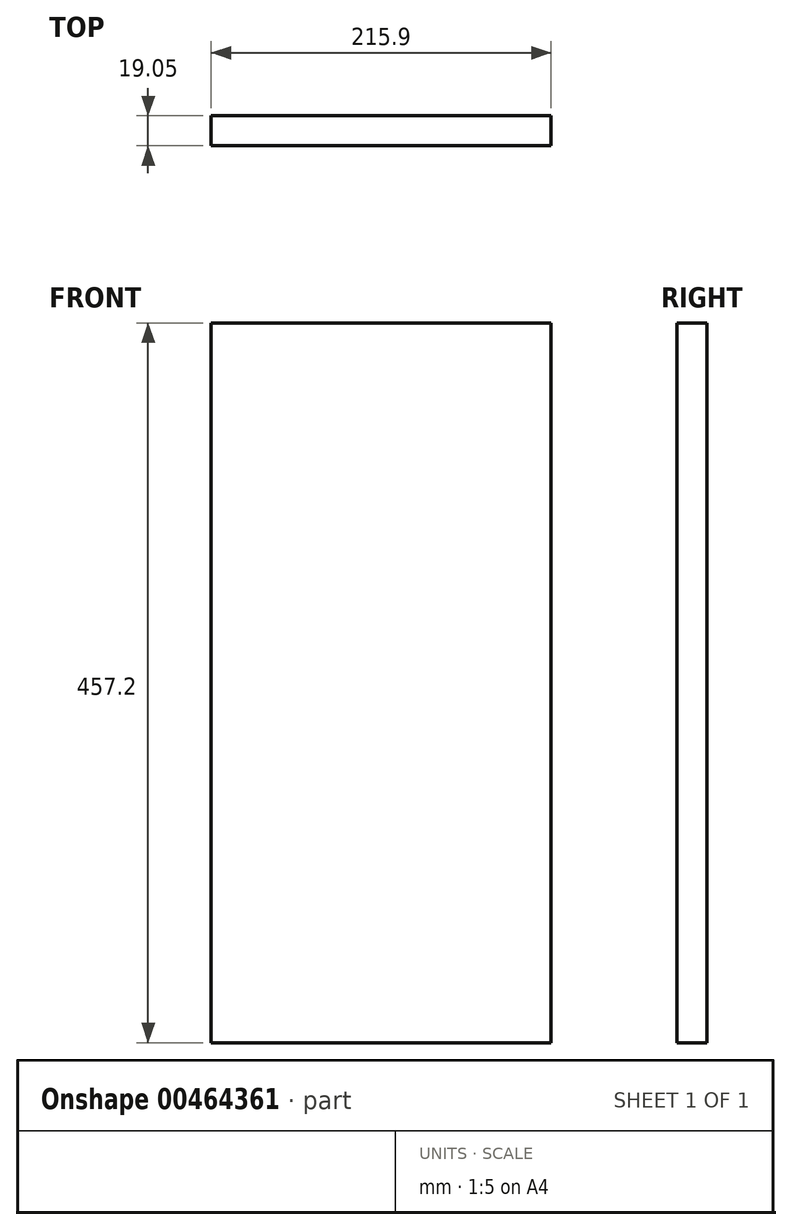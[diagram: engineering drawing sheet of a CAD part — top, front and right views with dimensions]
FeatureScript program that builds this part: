
annotation { "Feature Type Name" : "Feature", "Feature Type Description" : "" }
export const myFeature = defineFeature(function(context is Context, id is Id, definition is map)
    precondition{}
    {
        {
            var Q0;
            Q0=qCreatedBy(makeId("Front.planeOp"),FACE);
            var sketch = newSketch(context, id + "F0", { "sketchPlane" : qUnion([Q0])});
            skLineSegment(sketch, "E0", {"start": v(-104.24, 450.04) * mm, "end": v(111.66, 450.04) * mm});
            skLineSegment(sketch, "E1", {"start": v(-104.24, 450.04) * mm, "end": v(-104.24, -7.16) * mm});
            skLineSegment(sketch, "E2", {"start": v(-104.24, -7.16) * mm, "end": v(111.66, -7.16) * mm});
            skLineSegment(sketch, "E3", {"start": v(111.66, 450.04) * mm, "end": v(111.66, -7.16) * mm});
            skSolve(sketch);
        }
        {
            var Q0;
            Q0=makeQuery(id+"F0.imprint","IMPRINT",FACE,{"disambiguationData":[TD([[makeQuery(id+"F0.imprint","IMPRINT",EDGE,{"derivedFrom":sQuery(id+"F0.wireOp",EDGE,"E0")}),-1.0]])]});
            extrude(context, id + "F1", {"entities" : qUnion([Q0]), "depth" : 19.05 * mm});
        }
        {
            var Q0;
            Q0=makeQuery(id+"F1.opExtrude","CAP_FACE",FACE,{"disambiguationData":[OSD([sQuery(id+"F0.wireOp",EDGE,"E0"),sQuery(id+"F0.wireOp",EDGE,"E1"),sQuery(id+"F0.wireOp",EDGE,"E2"),sQuery(id+"F0.wireOp",EDGE,"E3")])],"isStart":false});
            var sketch = newSketch(context, id + "F2", { "sketchPlane" : qUnion([Q0])});
            skLineSegment(sketch, "E4", {"start": v(-89.44, 450.04) * mm, "end": v(-89.44, 340.58) * mm});
            skLineSegment(sketch, "E5", {"start": v(-89.44, 340.58) * mm, "end": v(92.64, 340.58) * mm});
            skLineSegment(sketch, "E6", {"start": v(92.64, 340.58) * mm, "end": v(92.64, 450.04) * mm});
            skSolve(sketch);
        }
        {
            var Q0;
            {var subQ0=sQuery(id+"F2.wireOp",EDGE,"E4");Q0=makeQuery(id+"F2.imprint","IMPRINT",FACE,{"disambiguationData":[TD([[makeQuery(id+"F2.imprint","IMPRINT",EDGE,{"derivedFrom":subQ0}),1.0]])]});}
            extrude(context, id + "F3", {"entities" : qUnion([Q0]), "operationType" : NewBodyOperationType.ADD, "depth" : -6.35 * mm});
        }
        {
            var Q0;
            Q0=makeQuery(id+"F1.opExtrude","CAP_FACE",FACE,{"disambiguationData":[OSD([sQuery(id+"F0.wireOp",EDGE,"E0"),sQuery(id+"F0.wireOp",EDGE,"E1"),sQuery(id+"F0.wireOp",EDGE,"E2"),sQuery(id+"F0.wireOp",EDGE,"E3")])],"isStart":false});
            var sketch = newSketch(context, id + "F4", { "sketchPlane" : qUnion([Q0])});
            skLineSegment(sketch, "E7", {"start": v(-92.07, 0) * mm, "end": v(96.33, 0) * mm});
            skLineSegment(sketch, "E8", {"start": v(96.33, 0) * mm, "end": v(96.33, 22.2) * mm});
            skLineSegment(sketch, "E9", {"start": v(96.33, 22.2) * mm, "end": v(-92.07, 22.2) * mm});
            skLineSegment(sketch, "E10", {"start": v(-92.07, 22.2) * mm, "end": v(-92.07, 0) * mm});
            skSolve(sketch);
        }
    });
